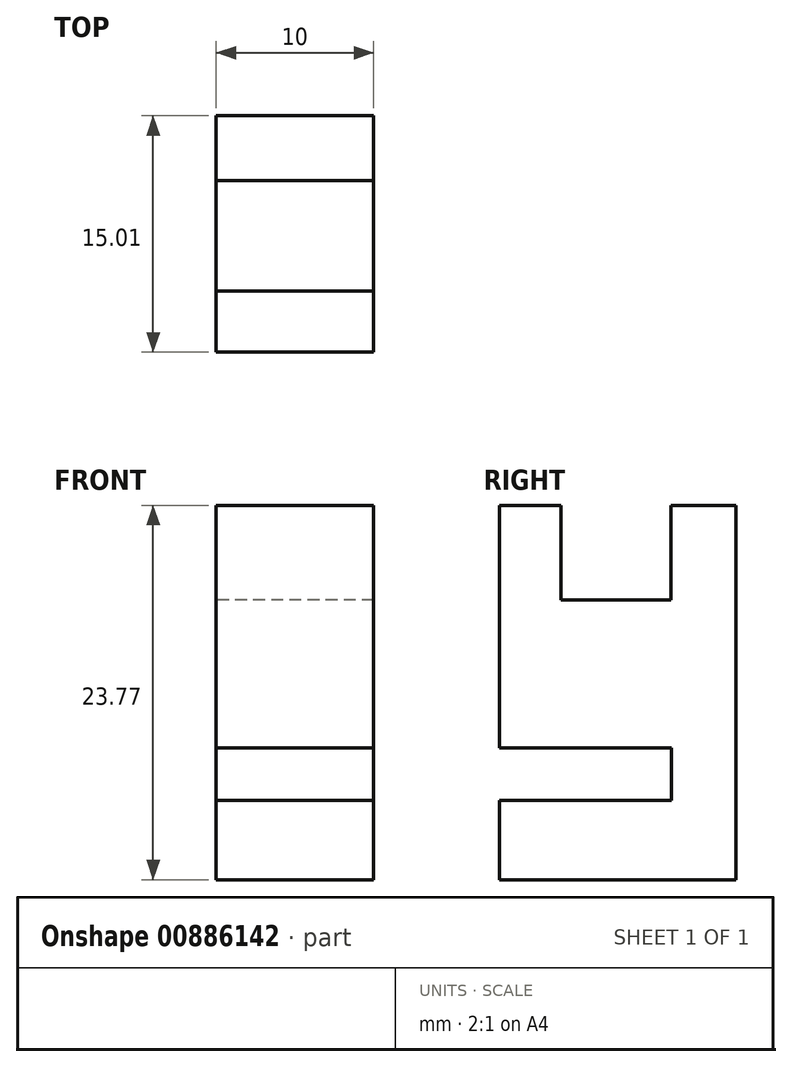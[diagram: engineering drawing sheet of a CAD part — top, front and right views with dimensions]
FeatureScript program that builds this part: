
annotation { "Feature Type Name" : "Feature", "Feature Type Description" : "" }
export const myFeature = defineFeature(function(context is Context, id is Id, definition is map)
    precondition{}
    {
        {
            var Q0;
            Q0=qCreatedBy(makeId("Right.planeOp"),FACE);
            var sketch = newSketch(context, id + "F0", { "sketchPlane" : qUnion([Q0])});
            skLineSegment(sketch, "E0", {"start": v(0, 0) * mm, "end": v(-15, 0) * mm});
            skLineSegment(sketch, "E1", {"start": v(-15, 0) * mm, "end": v(-15, 5.04) * mm});
            skLineSegment(sketch, "E2", {"start": v(-15, 5.04) * mm, "end": v(-4.1, 5.04) * mm});
            skLineSegment(sketch, "E3", {"start": v(-4.1, 5.04) * mm, "end": v(-4.1, 8.37) * mm});
            skLineSegment(sketch, "E4", {"start": v(-4.1, 8.37) * mm, "end": v(-15, 8.37) * mm});
            skLineSegment(sketch, "E5", {"start": v(-15, 8.37) * mm, "end": v(-15, 17.77) * mm});
            skLineSegment(sketch, "E6", {"start": v(-15, 17.77) * mm, "end": v(0, 17.77) * mm});
            skLineSegment(sketch, "E7", {"start": v(0, 17.77) * mm, "end": v(0, 0) * mm});
            skSolve(sketch);
        }
        {
            var Q0;
            Q0 = qSketchRegion(id + "F0", true);
            extrude(context, id + "F1", {"entities" : qUnion([Q0]), "depth" : 10 * mm, "offsetDistance" : 25 * mm});
        }
        {
            var Q0;
            Q0=makeQuery(id+"F1.opExtrude","SWEPT_FACE",FACE,{"disambiguationData":[OSD([sQuery(id+"F0.wireOp",EDGE,"E6")])]});
            var sketch = newSketch(context, id + "F2", { "sketchPlane" : qUnion([Q0])});
            skLineSegment(sketch, "E8.bottom", {"start": v(10, -11.12) * mm, "end": v(0, -11.12) * mm});
            skLineSegment(sketch, "E8.top", {"start": v(10, -4.12) * mm, "end": v(0, -4.12) * mm});
            skLineSegment(sketch, "E8.left", {"start": v(10, -11.12) * mm, "end": v(10, -4.12) * mm});
            skLineSegment(sketch, "E8.right", {"start": v(0, -11.12) * mm, "end": v(0, -4.12) * mm});
            skSolve(sketch);
        }
        {
            var Q0;
            {var subQ0=sQuery(id+"F2.wireOp",EDGE,"E8.top");Q0=makeQuery(id+"F2.imprint","IMPRINT",FACE,{"disambiguationData":[TD([[makeQuery(id+"F2.imprint","IMPRINT",EDGE,{"derivedFrom":subQ0}),-1.0]])]});}
            var Q1;
            {var subQ0=sQuery(id+"F2.wireOp",EDGE,"E8.bottom");Q1=makeQuery(id+"F2.imprint","IMPRINT",FACE,{"disambiguationData":[TD([[makeQuery(id+"F2.imprint","IMPRINT",EDGE,{"derivedFrom":subQ0}),1.0]])]});}
            extrude(context, id + "F3", {"entities" : qUnion([Q0, Q1]), "operationType" : NewBodyOperationType.ADD, "depth" : 6 * mm, "offsetDistance" : 25 * mm});
        }
    });
